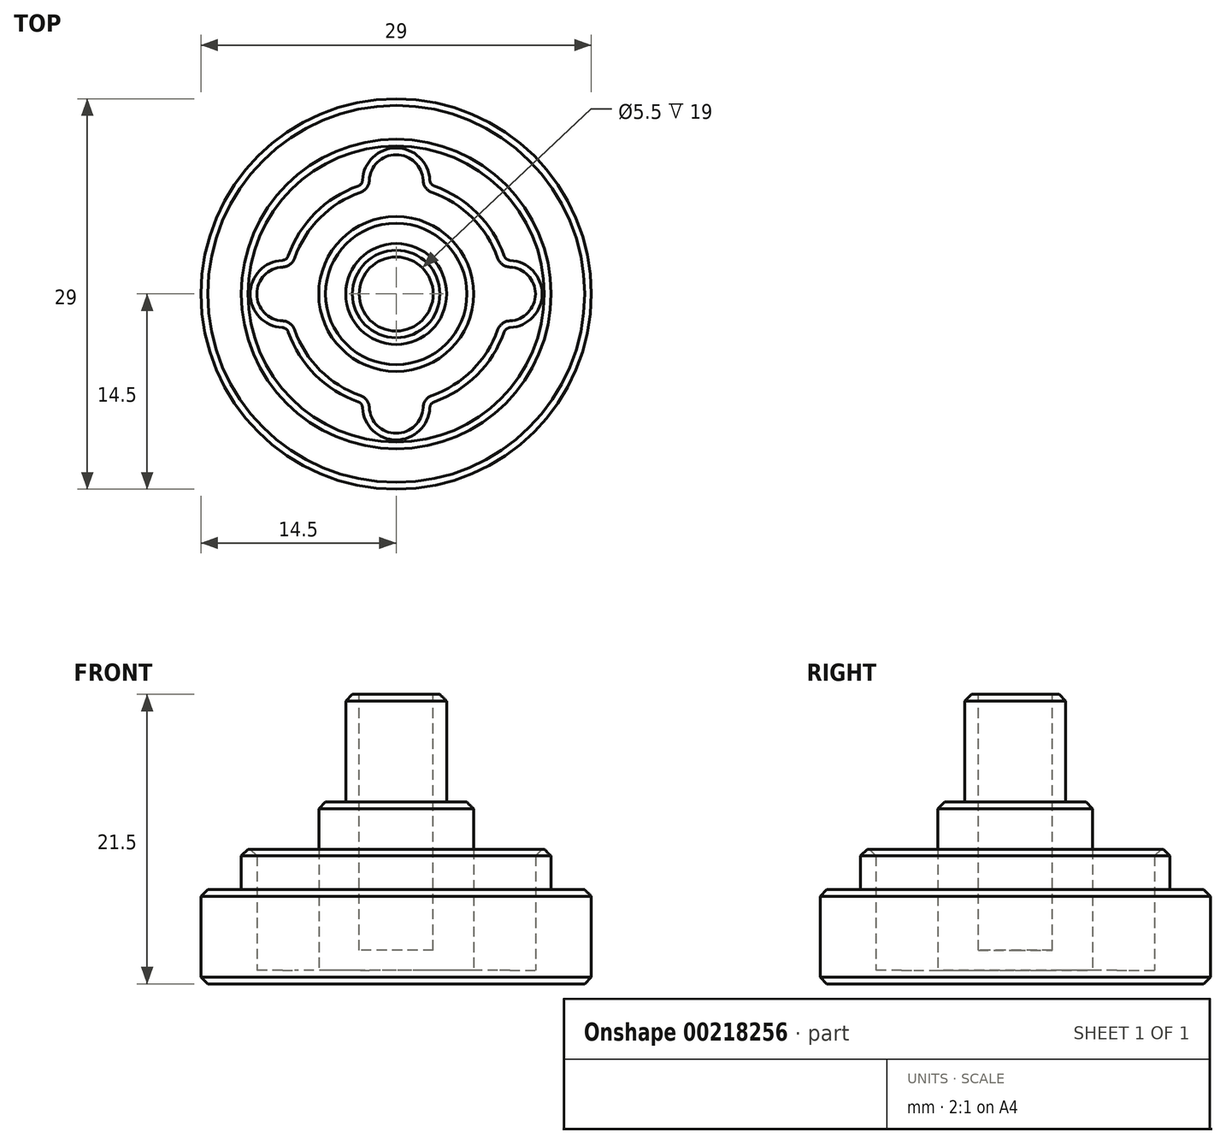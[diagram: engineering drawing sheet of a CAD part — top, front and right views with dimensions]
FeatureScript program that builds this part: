
annotation { "Feature Type Name" : "Feature", "Feature Type Description" : "" }
export const myFeature = defineFeature(function(context is Context, id is Id, definition is map)
    precondition{}
    {
        {
            var Q0;
            Q0=qCreatedBy(makeId("Top.planeOp"),FACE);
            var sketch = newSketch(context, id + "F0", { "sketchPlane" : qUnion([Q0])});
            skCircle(sketch, "E0", {"center": v(0, 0) * mm, "radius": 14.5 * mm});
            skSolve(sketch);
        }
        {
            var Q0;
            Q0=qSketchRegion(id+"F0",true);
            extrude(context, id + "F1", {"entities" : qUnion([Q0]), "depth" : 10 * mm});
        }
        {
            var Q0;
            Q0=makeQuery(id+"F1.opExtrude","CAP_FACE",FACE,{"disambiguationData":[OSD([sQuery(id+"F0.wireOp",EDGE,"E0")])],"isStart":false});
            var sketch = newSketch(context, id + "F2", { "sketchPlane" : qUnion([Q0])});
            skCircle(sketch, "E1", {"center": v(0, 0) * mm, "radius": 11.5 * mm});
            skCircle(sketch, "E2", {"center": v(0, 0) * mm, "radius": 8 * mm});
            skLineSegment(sketch, "E3", {"start": v(-2, 7.75) * mm, "end": v(-2, 8.35) * mm});
            skLineSegment(sketch, "E4", {"start": v(-2, 8.35) * mm, "end": v(2, 8.35) * mm});
            skLineSegment(sketch, "E5", {"start": v(2, 8.35) * mm, "end": v(2, 7.75) * mm});
            skArc(sketch, "E6", {"start": v(2, 8.35) * mm, "mid": v(0, 10.35) * mm, "end": v(-2, 8.35) * mm});
            skArc(sketch, "E7.1.0", {"start": v(-8.35, 2) * mm, "mid": v(-10.35, 0) * mm, "end": v(-8.35, -2) * mm});
            skLineSegment(sketch, "E7.1.1", {"start": v(-8.35, -2) * mm, "end": v(-8.35, 2) * mm});
            skLineSegment(sketch, "E7.1.2", {"start": v(-7.75, -2) * mm, "end": v(-8.35, -2) * mm});
            skLineSegment(sketch, "E7.1.3", {"start": v(-8.35, 2) * mm, "end": v(-7.75, 2) * mm});
            skArc(sketch, "E7.2.0", {"start": v(-2, -8.35) * mm, "mid": v(0, -10.35) * mm, "end": v(2, -8.35) * mm});
            skLineSegment(sketch, "E7.2.1", {"start": v(2, -8.35) * mm, "end": v(-2, -8.35) * mm});
            skArc(sketch, "E7.3.0", {"start": v(8.35, -2) * mm, "mid": v(10.35, 0) * mm, "end": v(8.35, 2) * mm});
            skLineSegment(sketch, "E7.3.1", {"start": v(8.35, 2) * mm, "end": v(8.35, -2) * mm});
            skLineSegment(sketch, "E7.3.2", {"start": v(7.75, 2) * mm, "end": v(8.35, 2) * mm});
            skLineSegment(sketch, "E8", {"start": v(8.35, -2) * mm, "end": v(7.75, -2) * mm});
            skLineSegment(sketch, "E9", {"start": v(-2, -8.35) * mm, "end": v(-2, -7.75) * mm});
            skLineSegment(sketch, "E10", {"start": v(2, -8.35) * mm, "end": v(2, -7.75) * mm});
            skSolve(sketch);
        }
        {
            var Q0;
            Q0=qSketchRegion(id+"F2",true);
            extrude(context, id + "F3", {"entities" : qUnion([Q0]), "operationType" : NewBodyOperationType.ADD, "depth" : 9 * mm});
        }
        {
            var Q0;
            {var subQ0=sQuery(id+"F0.wireOp",EDGE,"E0");Q0=makeQuery(id+"F3.boolean.opBoolean","SPLIT",FACE,{"disambiguationData":[TD([makeQuery(id+"F1.opExtrude","SWEPT_FACE",FACE,{"disambiguationData":[OSD([subQ0])]})])],"derivedFrom":makeQuery(id+"F1.opExtrude","CAP_FACE",FACE,{"disambiguationData":[OSD([subQ0])],"isStart":false})});}
            var sketch = newSketch(context, id + "F4", { "sketchPlane" : qUnion([Q0])});
            skCircle(sketch, "E11", {"center": v(0, 0) * mm, "radius": 14.5 * mm});
            skCircle(sketch, "E12", {"center": v(0, 0) * mm, "radius": 11.5 * mm});
            skSolve(sketch);
        }
        {
            var Q0;
            Q0=qSketchRegion(id+"F4",true);
            extrude(context, id + "F5", {"entities" : qUnion([Q0]), "operationType" : NewBodyOperationType.ADD, "depth" : 6 * mm});
        }
        {
            var Q0;
            Q0=makeQuery(id+"F1.opExtrude","CAP_FACE",FACE,{"disambiguationData":[OSD([sQuery(id+"F0.wireOp",EDGE,"E0")])],"isStart":true});
            var sketch = newSketch(context, id + "F6", { "sketchPlane" : qUnion([Q0])});
            skCircle(sketch, "E13", {"center": v(0, 0) * mm, "radius": 25 * mm});
            skSolve(sketch);
        }
        {
            var Q0;
            Q0=qSketchRegion(id+"F6",true);
            extrude(context, id + "F7", {"entities" : qUnion([Q0]), "operationType" : NewBodyOperationType.REMOVE, "oppositeDirection" : true, "depth" : 9 * mm});
        }
        {
            var Q0;
            Q0=makeQuery(id+"F3.opExtrude","SWEPT_EDGE",EDGE,{"disambiguationData":[OSD([sQuery(id+"F2.wireOp",EDGE,"E2"),sQuery(id+"F2.wireOp",EDGE,"E7.1.3")])]});
            var Q1;
            Q1=makeQuery(id+"F3.opExtrude","SWEPT_EDGE",EDGE,{"disambiguationData":[OSD([sQuery(id+"F2.wireOp",EDGE,"E2"),sQuery(id+"F2.wireOp",EDGE,"E3")])]});
            var Q2;
            Q2=makeQuery(id+"F3.opExtrude","SWEPT_EDGE",EDGE,{"disambiguationData":[OSD([sQuery(id+"F2.wireOp",EDGE,"E2"),sQuery(id+"F2.wireOp",EDGE,"E5")])]});
            var Q3;
            Q3=makeQuery(id+"F3.opExtrude","SWEPT_EDGE",EDGE,{"disambiguationData":[OSD([sQuery(id+"F2.wireOp",EDGE,"E2"),sQuery(id+"F2.wireOp",EDGE,"E7.3.2")])]});
            var Q4;
            Q4=makeQuery(id+"F3.opExtrude","SWEPT_EDGE",EDGE,{"disambiguationData":[OSD([sQuery(id+"F2.wireOp",EDGE,"E2"),sQuery(id+"F2.wireOp",EDGE,"E7.1.2")])]});
            var Q5;
            Q5=makeQuery(id+"F3.opExtrude","SWEPT_EDGE",EDGE,{"disambiguationData":[OSD([sQuery(id+"F2.wireOp",EDGE,"E2"),sQuery(id+"F2.wireOp",EDGE,"E7.2.3")])]});
            var Q6;
            Q6=makeQuery(id+"F3.opExtrude","SWEPT_EDGE",EDGE,{"disambiguationData":[OSD([sQuery(id+"F2.wireOp",EDGE,"E2"),sQuery(id+"F2.wireOp",EDGE,"E7.3.3")])]});
            var Q7;
            Q7=makeQuery(id+"F3.opExtrude","SWEPT_EDGE",EDGE,{"disambiguationData":[OSD([sQuery(id+"F2.wireOp",EDGE,"E2"),sQuery(id+"F2.wireOp",EDGE,"E7.2.2")])]});
            fillet(context, id + "F8", {"entities" : qUnion([Q0, Q1, Q2, Q3, Q4, Q5, Q6, Q7]), "radius" : 1 * mm, "tangentPropagation" : true, "allowEdgeOverflow" : false});
        }
        {
            var Q0;
            {var subQ6=sQuery(id+"F2.wireOp",EDGE,"E3");Q0=makeQuery(id+"F3.boolean.opBoolean","SPLIT",FACE,{"disambiguationData":[TD([makeQuery(id+"F3.opExtrude","SWEPT_FACE",FACE,{"disambiguationData":[OSD([subQ6])]})])],"derivedFrom":makeQuery(id+"F1.opExtrude","CAP_FACE",FACE,{"disambiguationData":[OSD([sQuery(id+"F0.wireOp",EDGE,"E0")])],"isStart":false})});}
            var sketch = newSketch(context, id + "F9", { "sketchPlane" : qUnion([Q0])});
            skCircle(sketch, "E14", {"center": v(0, 0) * mm, "radius": 5.75 * mm});
            skSolve(sketch);
        }
        {
            var Q0;
            Q0 = qSketchRegion(id + "F9", true);
            extrude(context, id + "F10", {"entities" : qUnion([Q0]), "operationType" : NewBodyOperationType.ADD, "depth" : 12.5 * mm});
        }
        {
            var Q0;
            Q0=makeQuery(id+"F10.opExtrude","CAP_FACE",FACE,{"disambiguationData":[OSD([sQuery(id+"F9.wireOp",EDGE,"E14")])],"isStart":false});
            var sketch = newSketch(context, id + "F11", { "sketchPlane" : qUnion([Q0])});
            skCircle(sketch, "E15", {"center": v(0, 0) * mm, "radius": 3.75 * mm});
            skSolve(sketch);
        }
        {
            var Q0;
            Q0 = qSketchRegion(id + "F11", true);
            extrude(context, id + "F12", {"entities" : qUnion([Q0]), "operationType" : NewBodyOperationType.ADD, "depth" : 8 * mm});
        }
        {
            var Q0;
            Q0=makeQuery(id+"F3.opExtrude","CAP_FACE",FACE,{"disambiguationData":[OSD([sQuery(id+"F2.wireOp",EDGE,"E1"),sQuery(id+"F2.wireOp",EDGE,"E2"),sQuery(id+"F2.wireOp",EDGE,"E3"),sQuery(id+"F2.wireOp",EDGE,"E5"),sQuery(id+"F2.wireOp",EDGE,"E6"),sQuery(id+"F2.wireOp",EDGE,"E7.1.0"),sQuery(id+"F2.wireOp",EDGE,"E7.1.2"),sQuery(id+"F2.wireOp",EDGE,"E7.1.3"),sQuery(id+"F2.wireOp",EDGE,"E7.2.0"),sQuery(id+"F2.wireOp",EDGE,"E7.2.2"),sQuery(id+"F2.wireOp",EDGE,"E7.2.3"),sQuery(id+"F2.wireOp",EDGE,"E7.3.0"),sQuery(id+"F2.wireOp",EDGE,"E7.3.2"),sQuery(id+"F2.wireOp",EDGE,"E7.3.3")])],"isStart":false});
            var Q1;
            Q1=makeQuery(id+"F5.opExtrude","CAP_EDGE",EDGE,{"disambiguationData":[OSD([sQuery(id+"F4.wireOp",EDGE,"E11")])],"isStart":false});
            var Q2;
            Q2=makeQuery(id+"F12.opExtrude","CAP_FACE",FACE,{"disambiguationData":[OSD([sQuery(id+"F11.wireOp",EDGE,"E15")])],"isStart":false});
            var Q3;
            Q3=makeQuery(id+"F10.opExtrude","CAP_EDGE",EDGE,{"disambiguationData":[OSD([sQuery(id+"F9.wireOp",EDGE,"E14")])],"isStart":false});
            var Q4;
            Q4=makeQuery(id+"F7.boolean.opBoolean","INTERSECT",EDGE,{"derivedFrom":[makeQuery(id+"F5.boolean.opBoolean","MERGE",FACE,{"derivedFrom":[makeQuery(id+"F1.opExtrude","SWEPT_FACE",FACE,{"disambiguationData":[OSD([sQuery(id+"F0.wireOp",EDGE,"E0")])]}),makeQuery(id+"F5.opExtrude","SWEPT_FACE",FACE,{"disambiguationData":[OSD([sQuery(id+"F4.wireOp",EDGE,"E11")])]})]}),makeQuery(id+"F7.opExtrude","CAP_FACE",FACE,{"disambiguationData":[OSD([sQuery(id+"F6.wireOp",EDGE,"E13")])],"isStart":false})]});
            chamfer(context, id + "F13", {"entities" : qUnion([Q0, Q1, Q2, Q3, Q4]), "width" : .5 * mm, "tangentPropagation" : true});
        }
        {
            var Q0;
            Q0=makeQuery(id+"F12.opExtrude","CAP_FACE",FACE,{"disambiguationData":[OSD([sQuery(id+"F11.wireOp",EDGE,"E15")])],"isStart":false});
            var sketch = newSketch(context, id + "F14", { "sketchPlane" : qUnion([Q0])});
            skCircle(sketch, "E16", {"center": v(0, 0) * mm, "radius": 2.75 * mm});
            skSolve(sketch);
        }
        {
            var Q0;
            Q0 = qSketchRegion(id + "F14", true);
            extrude(context, id + "F15", {"entities" : qUnion([Q0]), "operationType" : NewBodyOperationType.REMOVE, "oppositeDirection" : true, "depth" : 19 * mm});
        }
    });
